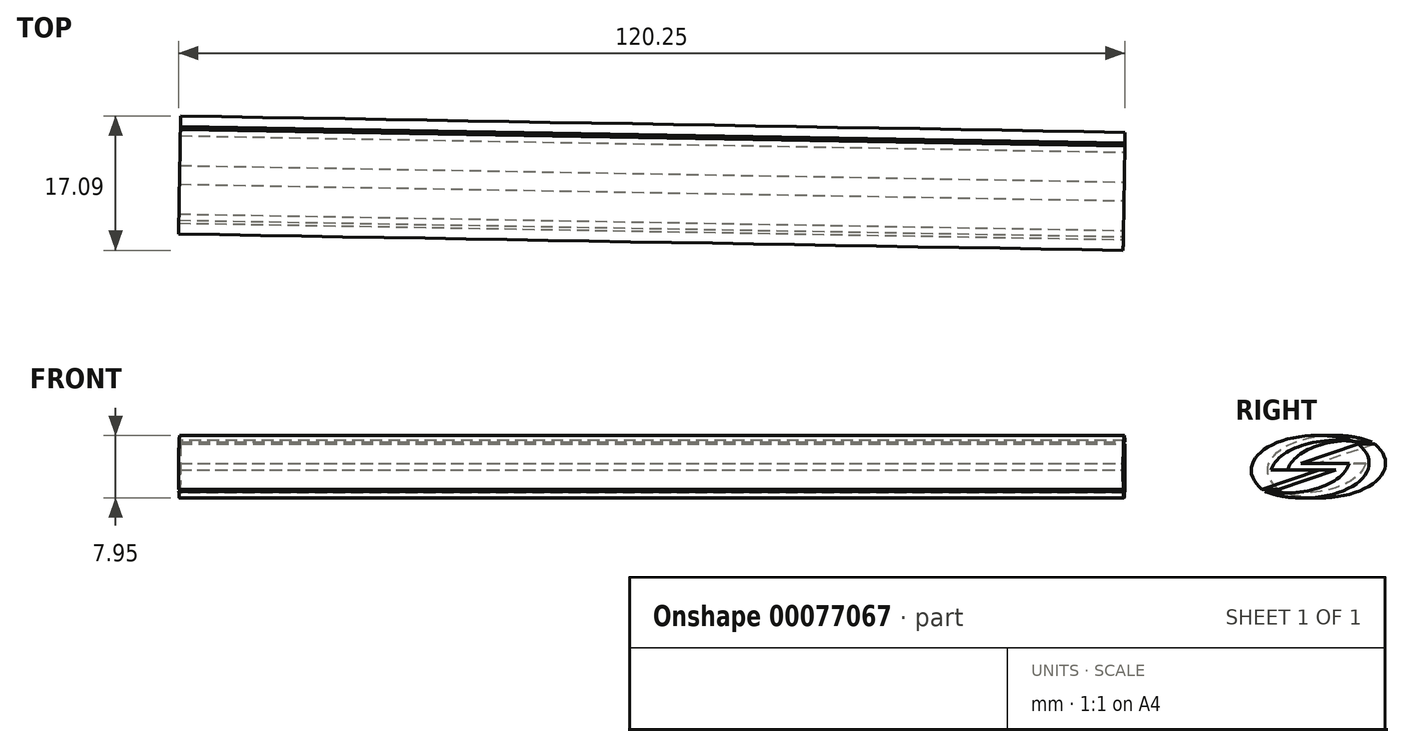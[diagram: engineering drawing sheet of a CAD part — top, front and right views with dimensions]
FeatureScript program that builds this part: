
annotation { "Feature Type Name" : "Feature", "Feature Type Description" : "" }
export const myFeature = defineFeature(function(context is Context, id is Id, definition is map)
    precondition{}
    {
        {
            var Q0;
            Q0=qCreatedBy(makeId("Front.planeOp"),FACE);
            var sketch = newSketch(context, id + "F0", { "sketchPlane" : qUnion([Q0])});
            skEllipticalArc(sketch, "E0", {});
            skLineSegment(sketch, "E1", {"start": v(0, 0) * mm, "end": v(4.1, 0) * mm});
            skLineSegment(sketch, "E2", {"start": v(4.88, -1.61) * mm, "end": v(0, 0) * mm});
            skEllipticalArc(sketch, "E3", {});
            skPoint(sketch, "E4.orphan", {"position": v(-5.41, 0) * mm});
            skPoint(sketch, "E5.orphan", {"position": v(5.8, 0) * mm});
            skEllipticalArc(sketch, "E6", {});
            skLineSegment(sketch, "E7", {"start": v(1.6, 0.59) * mm, "end": v(-2.51, 0.59) * mm});
            skLineSegment(sketch, "E8", {"start": v(-3.29, 2.2) * mm, "end": v(1.6, 0.59) * mm});
            skEllipticalArc(sketch, "E9", {});
            skPoint(sketch, "E10.orphan", {"position": v(-4.2, 0.59) * mm});
            const initialGuessF0  = {"E0": [0.00019164077152911984, 0, 1, 0, 0.005605491204728483, 0.0029456090684606678, 5.702943639447654, 2.1851302894137667], "E3": [-0.0014400467494755573, -0.0004161340610454776, 1, 0, 0.005605491204728483, 0.0029456090684606678, 0.14174686152028323, 1.8601439761282659], "E6": [0.0014026231809860835, 0.0005895231286726097, -1, 0, 0.005605491204728483, 0.0029456090684606678, 5.702943639447654, 2.1851302894137667], "E9": [0.003034310701990761, 0.0010056571897180866, -1, 0, 0.005605491204728483, 0.0029456090684606678, 0.14174686152028318, 1.8601439761282659]};
            skSetInitialGuess(sketch, initialGuessF0);
            skSolve(sketch);
        }
        {
            var Q0;
            Q0=makeQuery(id+"F0.imprint","IMPRINT",FACE,{"disambiguationData":[TD([[makeQuery(id+"F0.imprint","IMPRINT",EDGE,{"derivedFrom":sQuery(id+"F0.wireOp",EDGE,"E6")}),1.0]])]});
            var Q1;
            Q1=makeQuery(id+"F0.imprint","IMPRINT",FACE,{"disambiguationData":[TD([[makeQuery(id+"F0.imprint","IMPRINT",EDGE,{"derivedFrom":sQuery(id+"F0.wireOp",EDGE,"E0")}),1.0]])]});
            extrude(context, id + "F1", {"entities" : qUnion([Q0, Q1]), "depth" : 80 * mm, "offsetDistance" : 25 * mm});
        }
        {
            var Q0;
            Q0=qCreatedBy(makeId("Front.planeOp"),FACE);
            var sketch = newSketch(context, id + "F2", { "sketchPlane" : qUnion([Q0])});
            skLineSegment(sketch, "E11", {"start": v(0, 24) * mm, "end": v(0, -22.36) * mm});
            skSolve(sketch);
        }
        {
            var Q0;
            Q0=makeQuery(id+"F1.opExtrude","SWEPT_BODY",BODY,{"disambiguationData":[OSD([sQuery(id+"F0.wireOp",EDGE,"E6"),sQuery(id+"F0.wireOp",EDGE,"E7"),sQuery(id+"F0.wireOp",EDGE,"E8"),sQuery(id+"F0.wireOp",EDGE,"E9")])]});
            var Q1;
            Q1=makeQuery(id+"F1.opExtrude","SWEPT_BODY",BODY,{"disambiguationData":[OSD([sQuery(id+"F0.wireOp",EDGE,"E0"),sQuery(id+"F0.wireOp",EDGE,"E1"),sQuery(id+"F0.wireOp",EDGE,"E2"),sQuery(id+"F0.wireOp",EDGE,"E3")])]});
            var Q2;
            Q2=sQuery(id+"F2.wireOp",EDGE,"E11");
            transform(context, id + "F3", {"entities" : qUnion([Q0, Q1]), "transformType" : TransformType.ROTATION, "transformAxis" : qUnion([Q2]), "angle" : 91 * degree, "makeCopy" : false});
        }
        {
            var Q0;
            Q0=makeQuery(id+"F1.opExtrude","SWEPT_BODY",BODY,{"disambiguationData":[OSD([sQuery(id+"F0.wireOp",EDGE,"E0"),sQuery(id+"F0.wireOp",EDGE,"E1"),sQuery(id+"F0.wireOp",EDGE,"E2"),sQuery(id+"F0.wireOp",EDGE,"E3")])]});
            var Q1;
            Q1=makeQuery(id+"F1.opExtrude","SWEPT_BODY",BODY,{"disambiguationData":[OSD([sQuery(id+"F0.wireOp",EDGE,"E6"),sQuery(id+"F0.wireOp",EDGE,"E7"),sQuery(id+"F0.wireOp",EDGE,"E8"),sQuery(id+"F0.wireOp",EDGE,"E9")])]});
            var Q2;
            Q2=makeQuery(id+"F1.opExtrude","CAP_VERTEX",VERTEX,{"disambiguationData":[OSD([sQuery(id+"F0.wireOp",EDGE,"E7"),sQuery(id+"F0.wireOp",EDGE,"E8")])],"isStart":false});
            transform(context, id + "F4", {"entities" : qUnion([Q0, Q1]), "transformType" : TransformType.SCALE_UNIFORMLY, "scale" : 1.5, "scalePoint" : qUnion([Q2]), "makeCopy" : false});
        }
    });
